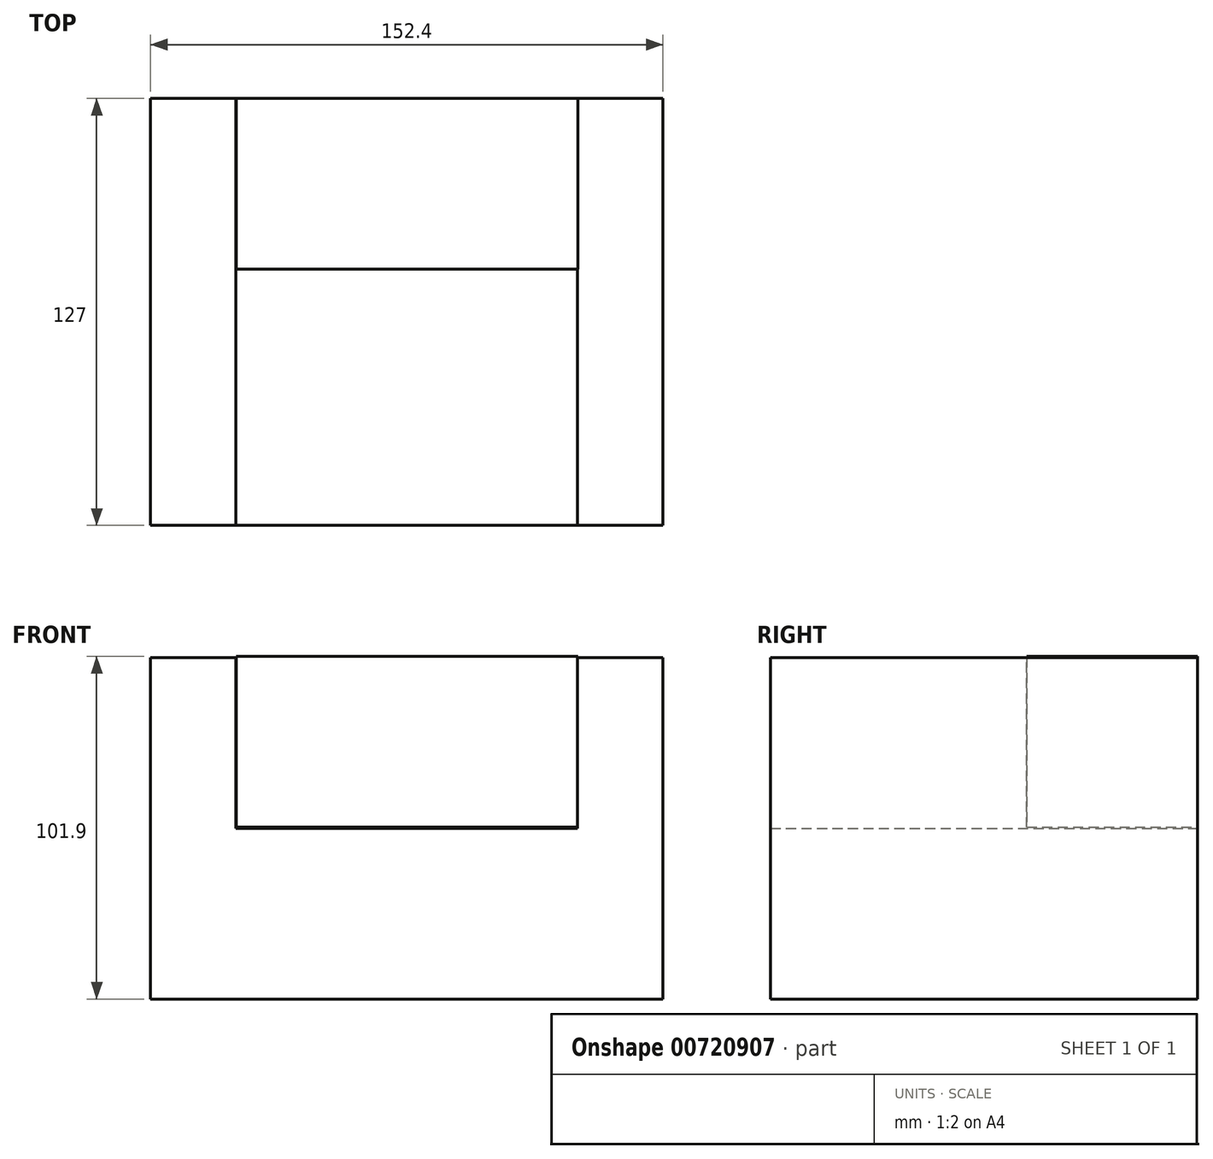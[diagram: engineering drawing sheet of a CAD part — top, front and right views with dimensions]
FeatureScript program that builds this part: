
annotation { "Feature Type Name" : "Feature", "Feature Type Description" : "" }
export const myFeature = defineFeature(function(context is Context, id is Id, definition is map)
    precondition{}
    {
        {
            var Q0;
            Q0=qCreatedBy(makeId("Front.planeOp"),FACE);
            var sketch = newSketch(context, id + "F0", { "sketchPlane" : qUnion([Q0])});
            skLineSegment(sketch, "E0", {"start": v(-73.15, -39.85) * mm, "end": v(79.25, -39.85) * mm});
            skLineSegment(sketch, "E1", {"start": v(-73.15, -39.85) * mm, "end": v(-73.15, 61.75) * mm});
            skLineSegment(sketch, "E2", {"start": v(79.25, -39.85) * mm, "end": v(79.25, 61.75) * mm});
            skLineSegment(sketch, "E3", {"start": v(79.25, 61.75) * mm, "end": v(53.85, 61.75) * mm});
            skLineSegment(sketch, "E4", {"start": v(53.85, 61.75) * mm, "end": v(53.85, 10.95) * mm});
            skLineSegment(sketch, "E5", {"start": v(-73.15, 61.75) * mm, "end": v(-47.75, 61.75) * mm});
            skLineSegment(sketch, "E6", {"start": v(-47.75, 61.75) * mm, "end": v(-47.75, 10.95) * mm});
            skLineSegment(sketch, "E7", {"start": v(-47.75, 10.95) * mm, "end": v(53.85, 10.95) * mm});
            skSolve(sketch);
        }
        {
            var Q0;
            Q0=qCreatedBy(makeId("Front.planeOp"),FACE);
            var sketch = newSketch(context, id + "F1", { "sketchPlane" : qUnion([Q0])});
            skLineSegment(sketch, "E8", {"start": v(-73.4, 62.05) * mm, "end": v(79, 62.05) * mm});
            skLineSegment(sketch, "E9", {"start": v(53.92, 62.05) * mm, "end": v(53.92, 11.24) * mm});
            skLineSegment(sketch, "E10", {"start": v(53.92, 11.24) * mm, "end": v(-47.68, 11.24) * mm});
            skLineSegment(sketch, "E11", {"start": v(-47.68, 11.24) * mm, "end": v(-47.68, 62.05) * mm});
            skSolve(sketch);
        }
        {
            var Q0;
            Q0=makeQuery(id+"F0.imprint","IMPRINT",FACE,{"disambiguationData":[TD([[makeQuery(id+"F0.imprint","IMPRINT",EDGE,{"derivedFrom":sQuery(id+"F0.wireOp",EDGE,"E0")}),1.0]])]});
            extrude(context, id + "F2", {"entities" : qUnion([Q0]), "depth" : 127 * mm, "offsetDistance" : 25.4 * mm});
        }
        {
            var Q0;
            {var subQ0=sQuery(id+"F1.wireOp",EDGE,"E9");Q0=makeQuery(id+"F1.imprint","IMPRINT",FACE,{"disambiguationData":[TD([[makeQuery(id+"F1.imprint","IMPRINT",EDGE,{"derivedFrom":subQ0}),-1.0]])]});}
            extrude(context, id + "F3", {"entities" : qUnion([Q0]), "operationType" : NewBodyOperationType.ADD, "depth" : 50.8 * mm, "offsetDistance" : 25.4 * mm});
        }
    });
